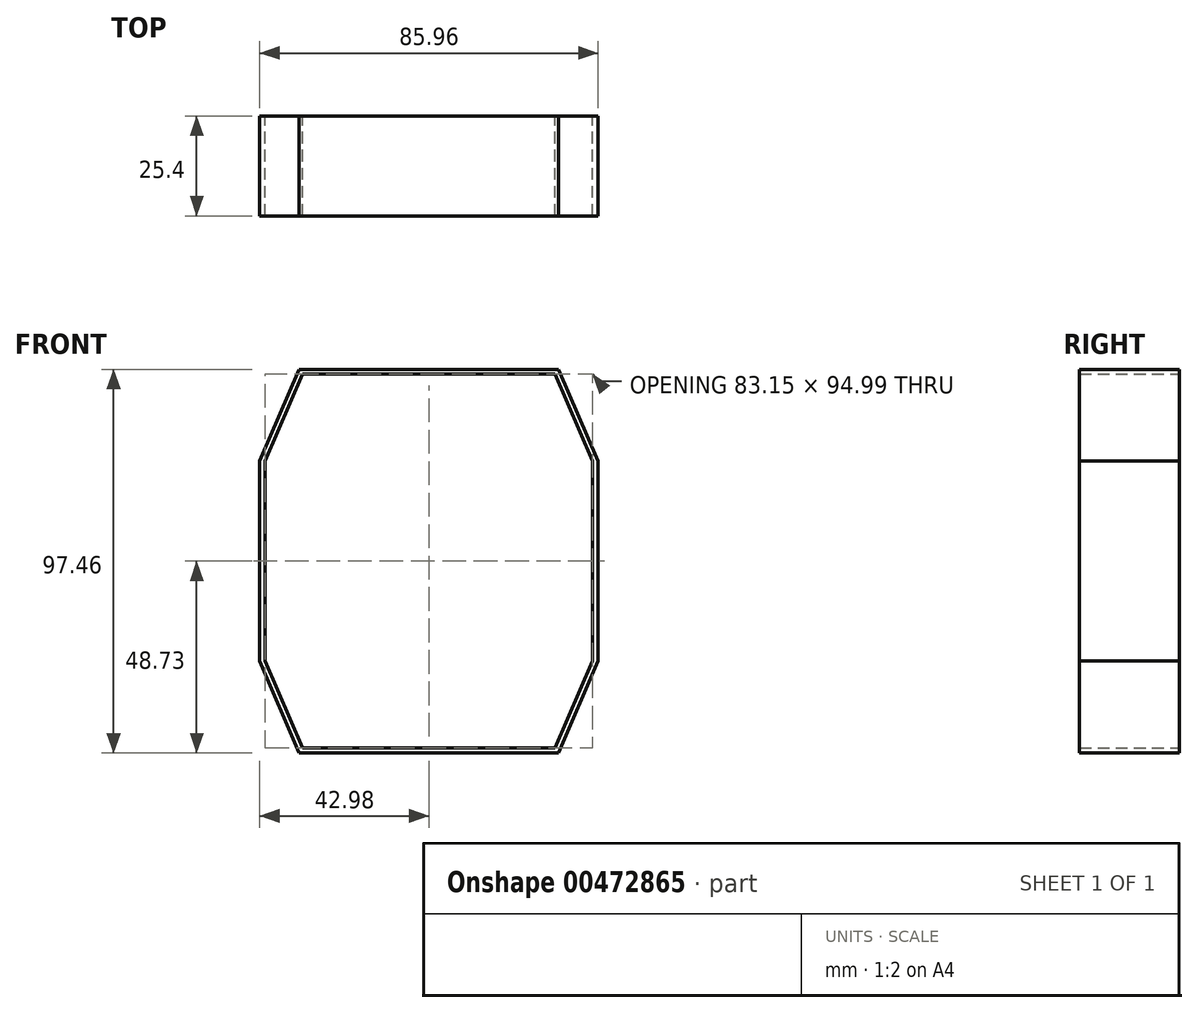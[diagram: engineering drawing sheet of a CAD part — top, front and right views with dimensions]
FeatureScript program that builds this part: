
annotation { "Feature Type Name" : "Feature", "Feature Type Description" : "" }
export const myFeature = defineFeature(function(context is Context, id is Id, definition is map)
    precondition{}
    {
        {
            var Q0;
            Q0=qCreatedBy(makeId("Front.planeOp"),FACE);
            var sketch = newSketch(context, id + "F0", { "sketchPlane" : qUnion([Q0])});
            skLineSegment(sketch, "E0", {"start": v(-32.06, 48.73) * mm, "end": v(32.94, 48.73) * mm});
            skLineSegment(sketch, "E1", {"start": v(32.94, 48.73) * mm, "end": v(42.98, 25.4) * mm});
            skLineSegment(sketch, "E2.MirrorCS", {"start": v(-32.94, 48.73) * mm, "end": v(-42.98, 25.4) * mm});
            skLineSegment(sketch, "E3.MirrorCS", {"start": v(32.06, 48.73) * mm, "end": v(-32.94, 48.73) * mm});
            skLineSegment(sketch, "E4.MirrorCS", {"start": v(-32.94, -48.73) * mm, "end": v(-42.98, -25.4) * mm});
            skLineSegment(sketch, "E5.MirrorCS", {"start": v(32.94, -48.73) * mm, "end": v(42.98, -25.4) * mm});
            skLineSegment(sketch, "E6.MirrorCS", {"start": v(32.06, -48.73) * mm, "end": v(-32.94, -48.73) * mm});
            skLineSegment(sketch, "E7", {"start": v(-42.98, 25.4) * mm, "end": v(-42.98, -25.4) * mm});
            skLineSegment(sketch, "E8.MirrorCS", {"start": v(42.98, 25.4) * mm, "end": v(42.98, -25.4) * mm});
            skLineSegment(sketch, "E9", {"start": v(-32.94, 48.73) * mm, "end": v(32.94, 48.73) * mm});
            skLineSegment(sketch, "E10", {"start": v(32.94, -48.73) * mm, "end": v(-32.94, -48.73) * mm});
            skLineSegment(sketch, "E11", {"start": v(-32.06, 47.5) * mm, "end": v(-41.57, 25.4) * mm});
            skLineSegment(sketch, "E12", {"start": v(-32.06, 47.5) * mm, "end": v(0, 47.5) * mm});
            skLineSegment(sketch, "E13.MirrorCS", {"start": v(32.06, 47.5) * mm, "end": v(0, 47.5) * mm});
            skLineSegment(sketch, "E14.MirrorCS", {"start": v(32.06, 47.5) * mm, "end": v(41.57, 25.4) * mm});
            skLineSegment(sketch, "E15.MirrorCS", {"start": v(32.06, -47.5) * mm, "end": v(0, -47.5) * mm});
            skLineSegment(sketch, "E16.MirrorCS", {"start": v(-32.06, -47.5) * mm, "end": v(-41.57, -25.4) * mm});
            skLineSegment(sketch, "E17.MirrorCS", {"start": v(32.06, -47.5) * mm, "end": v(41.57, -25.4) * mm});
            skLineSegment(sketch, "E18.MirrorCS", {"start": v(-32.06, -47.5) * mm, "end": v(0, -47.5) * mm});
            skLineSegment(sketch, "E19", {"start": v(-41.57, -25.4) * mm, "end": v(-41.57, 25.4) * mm});
            skLineSegment(sketch, "E20.MirrorCS", {"start": v(41.57, -25.4) * mm, "end": v(41.57, 25.4) * mm});
            skSolve(sketch);
        }
        {
            var Q0;
            {var subQ4=sQuery(id+"F0.wireOp",EDGE,"E1");Q0=makeQuery(id+"F0.imprint","IMPRINT",FACE,{"disambiguationData":[TD([[makeQuery(id+"F0.imprint","IMPRINT",EDGE,{"derivedFrom":subQ4}),-1.0]])]});}
            extrude(context, id + "F1", {"entities" : qUnion([Q0]), "endBound" : BoundingType.SYMMETRIC, "depth" : 25.4 * mm});
        }
    });
